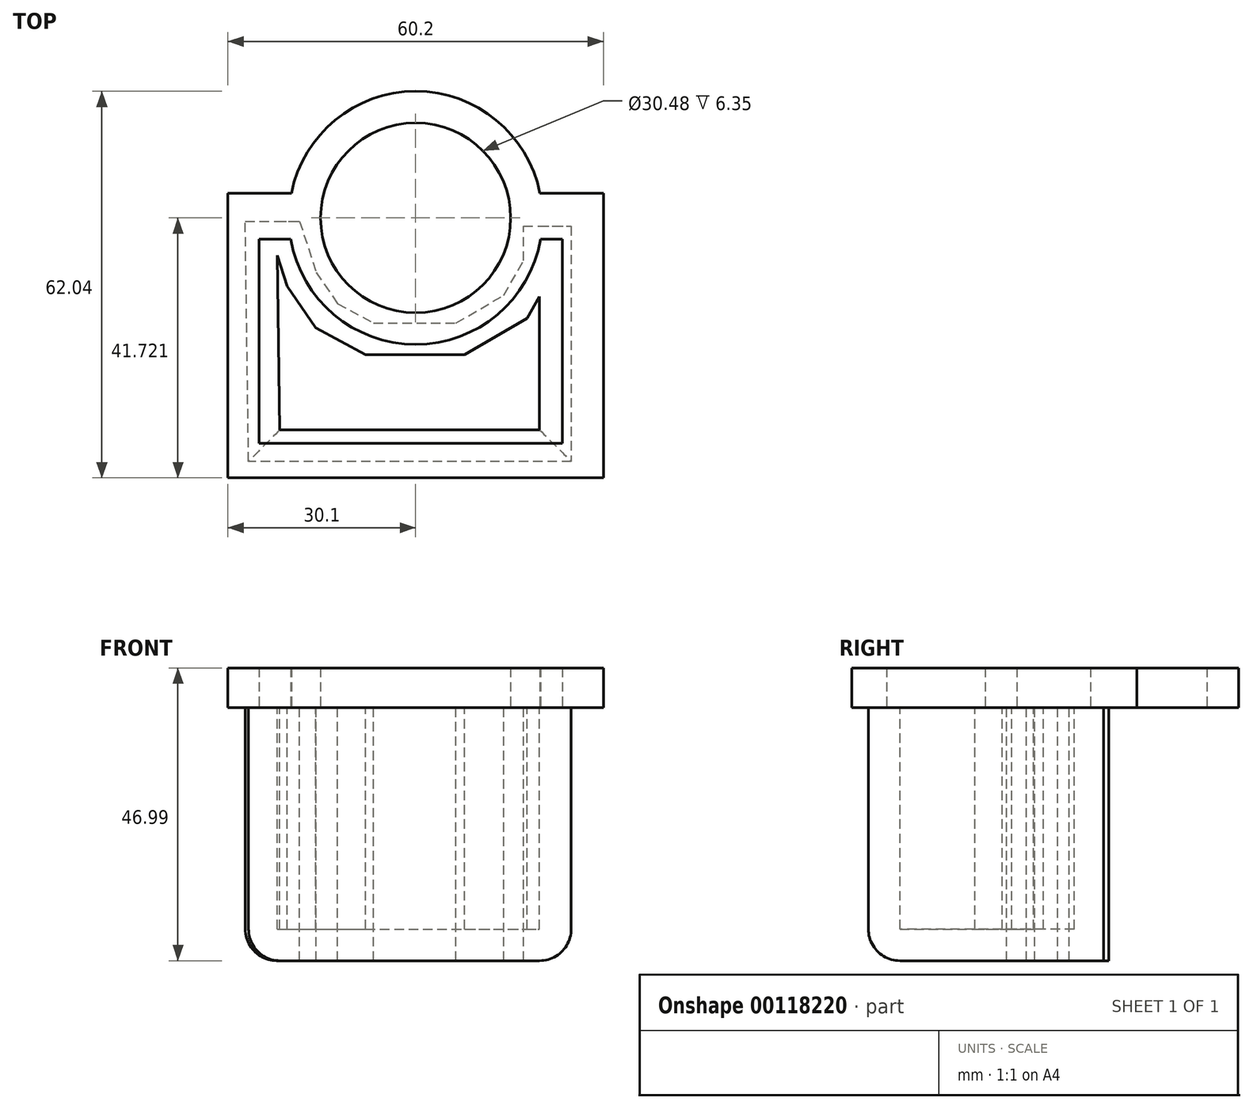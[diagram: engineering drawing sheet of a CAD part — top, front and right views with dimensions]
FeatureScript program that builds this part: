
annotation { "Feature Type Name" : "Feature", "Feature Type Description" : "" }
export const myFeature = defineFeature(function(context is Context, id is Id, definition is map)
    precondition{}
    {
        {
            var Q0;
            Q0=qCreatedBy(makeId("Top.planeOp"),FACE);
            var sketch = newSketch(context, id + "F0", { "sketchPlane" : qUnion([Q0])});
            skCircle(sketch, "E0", {"center": v(0, 30.63) * mm, "radius": 15.24 * mm});
            skArc(sketch, "E1", {"start": v(19.93, 34.6) * mm, "mid": v(0, 50.95) * mm, "end": v(-19.93, 34.6) * mm});
            skLineSegment(sketch, "E2.bottom", {"start": v(30.1, 34.6) * mm, "end": v(19.93, 34.6) * mm});
            skLineSegment(sketch, "E2.top", {"start": v(30.1, -11.1) * mm, "end": v(-30.1, -11.1) * mm});
            skLineSegment(sketch, "E2.left", {"start": v(30.1, 34.6) * mm, "end": v(30.1, -11.1) * mm});
            skLineSegment(sketch, "E2.right", {"start": v(-30.1, 34.6) * mm, "end": v(-30.1, -11.1) * mm});
            skLineSegment(sketch, "E3.bottom", {"start": v(-25.09, 27.2) * mm, "end": v(-20.03, 27.2) * mm});
            skLineSegment(sketch, "E3.top", {"start": v(-25.09, -5.55) * mm, "end": v(23.5, -5.55) * mm});
            skLineSegment(sketch, "E3.left", {"start": v(-25.09, 27.2) * mm, "end": v(-25.09, -5.55) * mm});
            skLineSegment(sketch, "E3.right", {"start": v(23.5, 27.2) * mm, "end": v(23.5, -5.55) * mm});
            skLineSegment(sketch, "E4.trimOffspring", {"start": v(20.03, 27.2) * mm, "end": v(23.5, 27.2) * mm});
            skLineSegment(sketch, "E5.trimOffspring", {"start": v(-19.93, 34.6) * mm, "end": v(-30.1, 34.6) * mm});
            skArc(sketch, "E6.trimOffspring", {"start": v(-20.03, 27.2) * mm, "mid": v(0, 10.31) * mm, "end": v(20.03, 27.2) * mm});
            skSolve(sketch);
        }
        {
            var Q0;
            Q0=makeQuery(id+"F0.imprint","IMPRINT",FACE,{"disambiguationData":[TD([[makeQuery(id+"F0.imprint","IMPRINT",EDGE,{"derivedFrom":sQuery(id+"F0.wireOp",EDGE,"E0")}),-1.0]])]});
            extrude(context, id + "F1", {"entities" : qUnion([Q0]), "depth" : 6.35 * mm});
        }
        {
            var Q0;
            Q0=qCreatedBy(makeId("Top.planeOp"),FACE);
            var sketch = newSketch(context, id + "F2", { "sketchPlane" : qUnion([Q0])});
            skLineSegment(sketch, "E7", {"start": v(-27.33, 30.1) * mm, "end": v(-18.62, 30.1) * mm});
            skLineSegment(sketch, "E8", {"start": v(-18.62, 30.1) * mm, "end": v(-15.98, 21.92) * mm});
            skLineSegment(sketch, "E9", {"start": v(-15.98, 21.92) * mm, "end": v(-12.54, 16.9) * mm});
            skLineSegment(sketch, "E10", {"start": v(-12.54, 16.9) * mm, "end": v(-6.73, 13.73) * mm});
            skLineSegment(sketch, "E11", {"start": v(-6.73, 13.73) * mm, "end": v(0, 13.73) * mm});
            skLineSegment(sketch, "E12", {"start": v(0, 13.73) * mm, "end": v(6.47, 13.73) * mm});
            skLineSegment(sketch, "E13", {"start": v(6.47, 13.73) * mm, "end": v(14.13, 18.22) * mm});
            skLineSegment(sketch, "E14", {"start": v(14.13, 18.22) * mm, "end": v(17.3, 23.77) * mm});
            skLineSegment(sketch, "E15", {"start": v(17.3, 23.77) * mm, "end": v(17.3, 29.31) * mm});
            skLineSegment(sketch, "E16", {"start": v(17.3, 29.31) * mm, "end": v(24.95, 29.31) * mm});
            skLineSegment(sketch, "E17", {"start": v(24.95, 29.31) * mm, "end": v(24.95, -8.45) * mm});
            skLineSegment(sketch, "E18", {"start": v(24.95, -8.45) * mm, "end": v(-26.8, -8.45) * mm});
            skLineSegment(sketch, "E19", {"start": v(-26.8, -8.45) * mm, "end": v(-27.33, 30.1) * mm});
            skSolve(sketch);
        }
        {
            var Q0;
            Q0=makeQuery(id+"F2.imprint","IMPRINT",FACE,{"disambiguationData":[TD([[makeQuery(id+"F2.imprint","IMPRINT",EDGE,{"derivedFrom":sQuery(id+"F2.wireOp",EDGE,"E7")}),-1.0]])]});
            extrude(context, id + "F3", {"entities" : qUnion([Q0]), "operationType" : NewBodyOperationType.ADD, "oppositeDirection" : true, "depth" : 40.64 * mm});
        }
        {
            var Q0;
            Q0=makeQuery(id+"F3.opExtrude","CAP_EDGE",EDGE,{"disambiguationData":[OSD([sQuery(id+"F2.wireOp",EDGE,"E17")])],"isStart":false});
            var Q1;
            Q1=makeQuery(id+"F3.opExtrude","CAP_EDGE",EDGE,{"disambiguationData":[OSD([sQuery(id+"F2.wireOp",EDGE,"E18")])],"isStart":false});
            var Q2;
            Q2=makeQuery(id+"F3.opExtrude","CAP_EDGE",EDGE,{"disambiguationData":[OSD([sQuery(id+"F2.wireOp",EDGE,"E19")])],"isStart":false});
            fillet(context, id + "F4", {"entities" : qUnion([Q0, Q1, Q2]), "radius" : 5.08 * mm, "tangentPropagation" : true, "allowEdgeOverflow" : false});
        }
        {
            var Q0;
            Q0=makeQuery(id+"F3.opExtrude","CAP_FACE",FACE,{"disambiguationData":[OSD([sQuery(id+"F2.wireOp",EDGE,"E7"),sQuery(id+"F2.wireOp",EDGE,"E8"),sQuery(id+"F2.wireOp",EDGE,"E9"),sQuery(id+"F2.wireOp",EDGE,"E10"),sQuery(id+"F2.wireOp",EDGE,"E11"),sQuery(id+"F2.wireOp",EDGE,"E12"),sQuery(id+"F2.wireOp",EDGE,"E13"),sQuery(id+"F2.wireOp",EDGE,"E14"),sQuery(id+"F2.wireOp",EDGE,"E15"),sQuery(id+"F2.wireOp",EDGE,"E16"),sQuery(id+"F2.wireOp",EDGE,"E17"),sQuery(id+"F2.wireOp",EDGE,"E18"),sQuery(id+"F2.wireOp",EDGE,"E19")])],"isStart":true});
            shell(context, id + "F5", {"entities" : qUnion([Q0]), "thickness" : 5.08 * mm});
        }
    });
